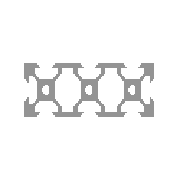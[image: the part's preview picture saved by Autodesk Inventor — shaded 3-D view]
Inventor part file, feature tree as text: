
AUTODESK INVENTOR PART (.ipt)
format: ipt  version: 2013 SP2 (Build 170200200, 200)  size: 228,352 bytes
history: native  units: mm
features: other x3, sketch x3, plane x1
ambient origin geometry x8: Origin, YZ Plane, XZ Plane, XY Plane, X Axis, Y Axis, Z Axis, Center Point
bodies: Solid1 (feature_tree), Body (feature_tree)
feature tree (7):
  other  "Driven Length"
  other  "Start Plane"
  other  "End Plane"
  sketch  "Sketch1"  dims[d0=10.0mm]
  sketch  "Sketch4"  dims[d1=10.0mm]
  plane  "Work Plane4"
  sketch  "Sketch5"  dims[d2=10.0mm d3=4.2mm d4=1.5mm d5=45.0deg d6=1.64mm d7=1.8mm d8=10.0mm d9=2.84mm d11=135.0deg d12=1.96mm d13=5.68mm d14=1.8mm d17=-0.0mm d18=10.0mm d19=0.13mm d20=0.0mm d23=90.0deg d22=10.0mm]
